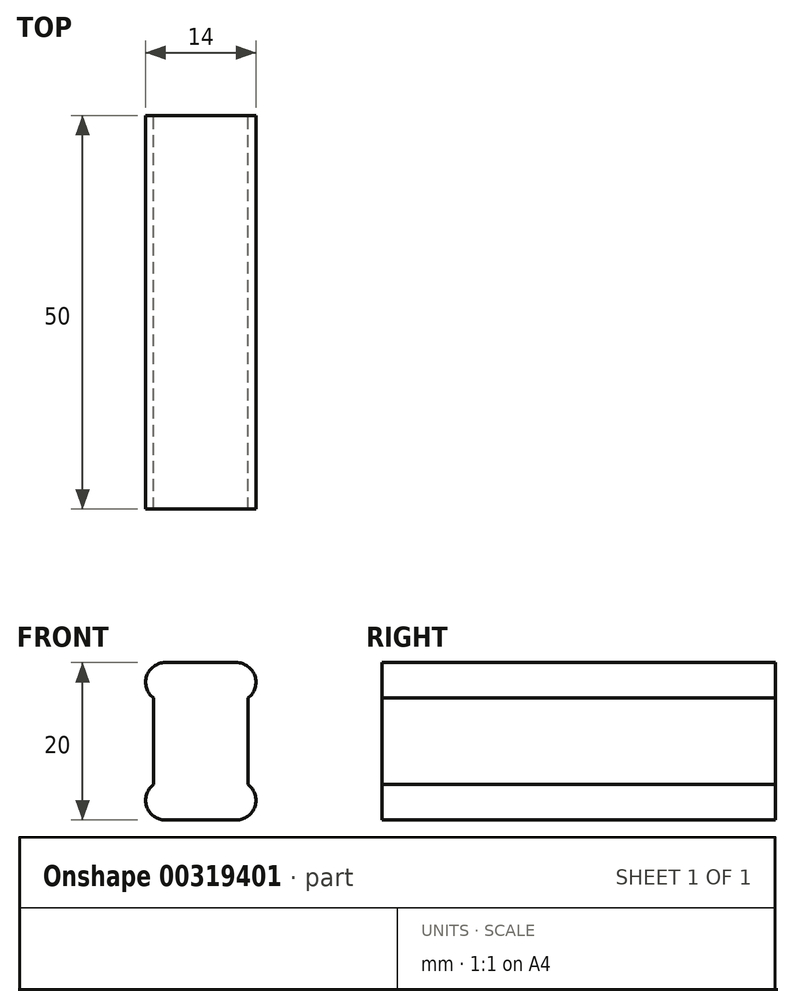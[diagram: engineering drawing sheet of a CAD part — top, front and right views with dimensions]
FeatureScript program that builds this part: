
annotation { "Feature Type Name" : "Feature", "Feature Type Description" : "" }
export const myFeature = defineFeature(function(context is Context, id is Id, definition is map)
    precondition{}
    {
        {
            var Q0;
            Q0=qCreatedBy(makeId("Front.planeOp"),FACE);
            var sketch = newSketch(context, id + "F0", { "sketchPlane" : qUnion([Q0])});
            skLineSegment(sketch, "E0", {"start": v(0, -24.32) * mm, "end": v(0, 16.86) * mm, "construction": true});
            skLineSegment(sketch, "E1.bottom", {"start": v(-4.5, 10) * mm, "end": v(4.5, 10) * mm});
            skLineSegment(sketch, "E1.top", {"start": v(-4.5, -10) * mm, "end": v(4.5, -10) * mm});
            skPoint(sketch, "E1.middle", {"position": v(0, 0) * mm});
            skLineSegment(sketch, "E2", {"start": v(-27.5, 0) * mm, "end": v(27.5, 0) * mm, "construction": true});
            skLineSegment(sketch, "E3", {"start": v(-4.5, 7.5) * mm, "end": v(4.5, 7.5) * mm, "construction": true});
            skPoint(sketch, "E4", {"position": v(0, 7.5) * mm});
            skArc(sketch, "E5.0.startCap", {"start": v(-6, 5.5) * mm, "mid": v(-6.87, 8.3) * mm, "end": v(-4.5, 10) * mm});
            skArc(sketch, "E5.0.endCap", {"start": v(4.5, 10) * mm, "mid": v(6.87, 8.3) * mm, "end": v(6, 5.5) * mm});
            skArc(sketch, "E6.MirrorCS", {"start": v(-6, -5.5) * mm, "mid": v(-6.87, -8.3) * mm, "end": v(-4.5, -10) * mm});
            skArc(sketch, "E7.MirrorCS", {"start": v(4.5, -10) * mm, "mid": v(6.87, -8.3) * mm, "end": v(6, -5.5) * mm});
            skLineSegment(sketch, "E8.MirrorCS", {"start": v(-4.5, -7.5) * mm, "end": v(4.5, -7.5) * mm, "construction": true});
            skPoint(sketch, "E9.trimOffspring.end.orphan", {"position": v(-6.06, -10) * mm});
            skPoint(sketch, "E10.orphan", {"position": v(5.85, -10) * mm});
            skPoint(sketch, "E11.orphan", {"position": v(4.5, -5) * mm});
            skPoint(sketch, "E12.orphan", {"position": v(-4.5, -5) * mm});
            skPoint(sketch, "E13.orphan", {"position": v(4.5, 5) * mm});
            skLineSegment(sketch, "E14.trimOffspring", {"start": v(6, 5.5) * mm, "end": v(6, -5.5) * mm});
            skPoint(sketch, "E1.right.start.orphan", {"position": v(6.06, 10) * mm});
            skLineSegment(sketch, "E15.trimOffspring", {"start": v(-6, 5.5) * mm, "end": v(-6, -5.5) * mm});
            skPoint(sketch, "E16.orphan", {"position": v(-4.5, 5) * mm});
            skPoint(sketch, "E17.orphan", {"position": v(-5.85, 10) * mm});
            skSolve(sketch);
        }
        {
            var Q0;
            Q0 = qSketchRegion(id + "F0", true);
            extrude(context, id + "F1", {"entities" : qUnion([Q0]), "endBound" : BoundingType.SYMMETRIC, "depth" : 50 * mm});
        }
    });
